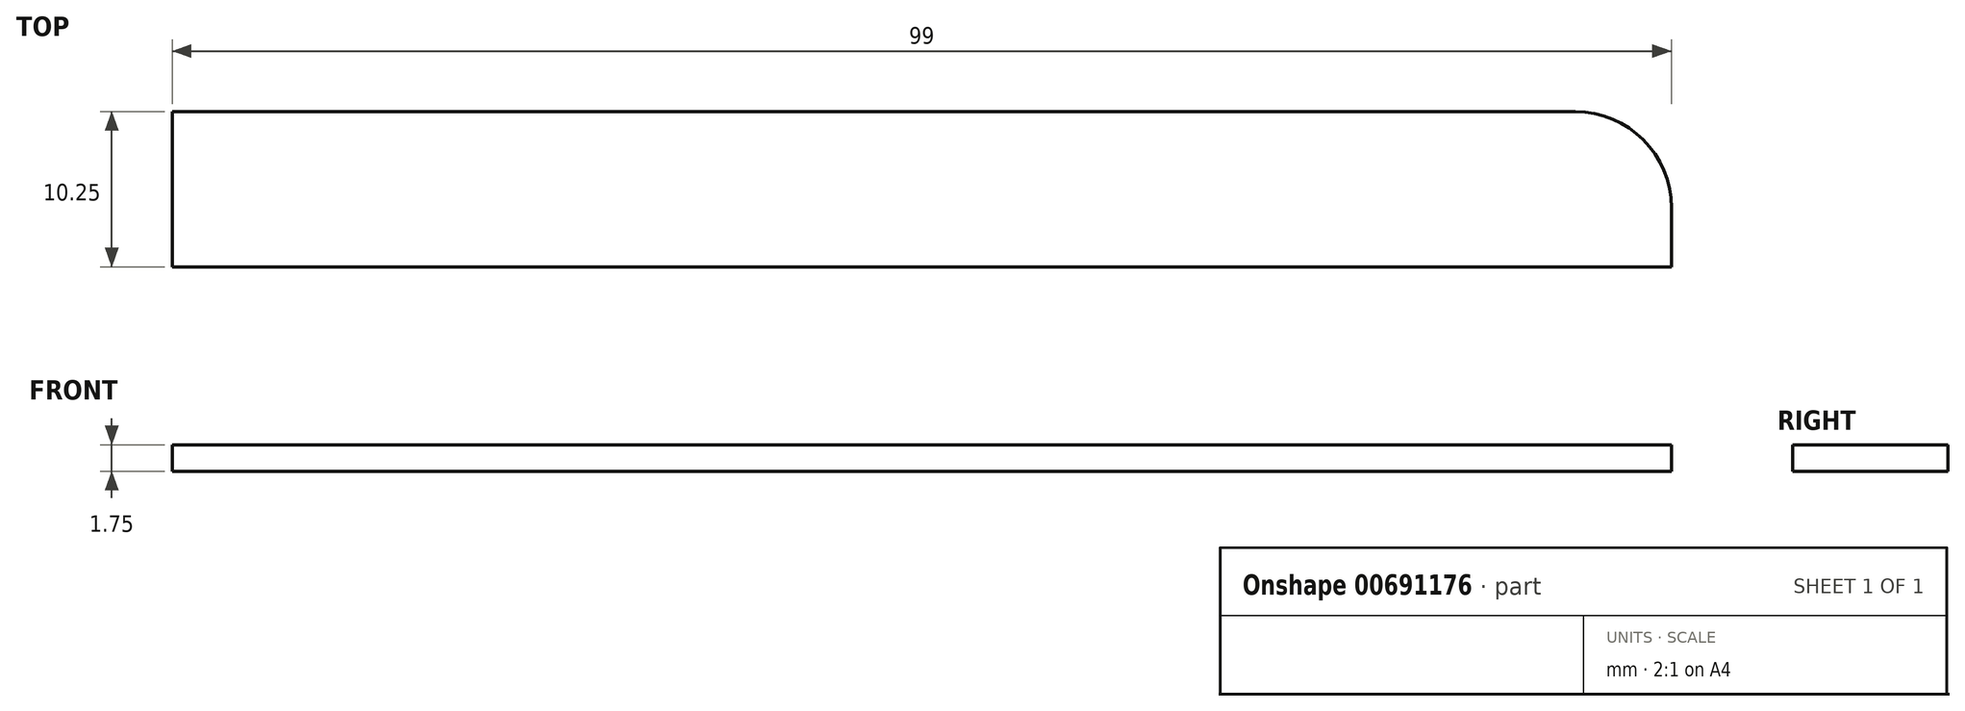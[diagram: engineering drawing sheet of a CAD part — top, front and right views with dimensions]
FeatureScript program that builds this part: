
annotation { "Feature Type Name" : "Feature", "Feature Type Description" : "" }
export const myFeature = defineFeature(function(context is Context, id is Id, definition is map)
    precondition{}
    {
        {
            var Q0;
            Q0=qCreatedBy(makeId("Top.planeOp"),FACE);
            var sketch = newSketch(context, id + "F0", { "sketchPlane" : qUnion([Q0])});
            skLineSegment(sketch, "E0.bottom", {"start": v(0, 0) * mm, "end": v(174, 0) * mm});
            skLineSegment(sketch, "E0.top", {"start": v(0, 34.5) * mm, "end": v(174, 34.5) * mm});
            skLineSegment(sketch, "E0.left", {"start": v(0, 0) * mm, "end": v(0, 34.5) * mm});
            skLineSegment(sketch, "E0.right", {"start": v(174, 0) * mm, "end": v(174, 34.5) * mm});
            skLineSegment(sketch, "E1.bottom", {"start": v(0, 0) * mm, "end": v(99, 0) * mm});
            skLineSegment(sketch, "E1.top", {"start": v(0, 10.25) * mm, "end": v(92.65, 10.25) * mm});
            skLineSegment(sketch, "E1.left", {"start": v(0, 0) * mm, "end": v(0, 10.25) * mm});
            skLineSegment(sketch, "E1.right", {"start": v(99, 0) * mm, "end": v(99, 3.9) * mm});
            skLineSegment(sketch, "E2.bottom", {"start": v(0, 34.5) * mm, "end": v(99, 34.5) * mm});
            skLineSegment(sketch, "E2.top", {"start": v(0, 24.25) * mm, "end": v(92.65, 24.25) * mm});
            skLineSegment(sketch, "E2.left", {"start": v(0, 34.5) * mm, "end": v(0, 24.25) * mm});
            skLineSegment(sketch, "E2.right", {"start": v(99, 34.5) * mm, "end": v(99, 30.6) * mm});
            skPoint(sketch, "E3.visualSharp", {"position": v(99, 10.25) * mm});
            skArc(sketch, "E3.filletArc", {"start": v(99, 3.9) * mm, "mid": v(97.14, 8.4) * mm, "end": v(92.65, 10.25) * mm});
            skPoint(sketch, "E4.visualSharp", {"position": v(99, 24.25) * mm});
            skArc(sketch, "E4.filletArc", {"start": v(92.65, 24.25) * mm, "mid": v(97.14, 26.1) * mm, "end": v(99, 30.6) * mm});
            skSolve(sketch);
        }
        {
            var Q0;
            Q0=makeQuery(id+"F0.imprint","IMPRINT",FACE,{"disambiguationData":[TD([[makeQuery(id+"F0.imprint","IMPRINT",EDGE,{"derivedFrom":sQuery(id+"F0.wireOp",EDGE,"E0.bottom")}),1.0]])]});
            extrude(context, id + "F1", {"entities" : qUnion([Q0]), "depth" : 1.75 * mm, "offsetDistance" : 25.4 * mm});
        }
    });
